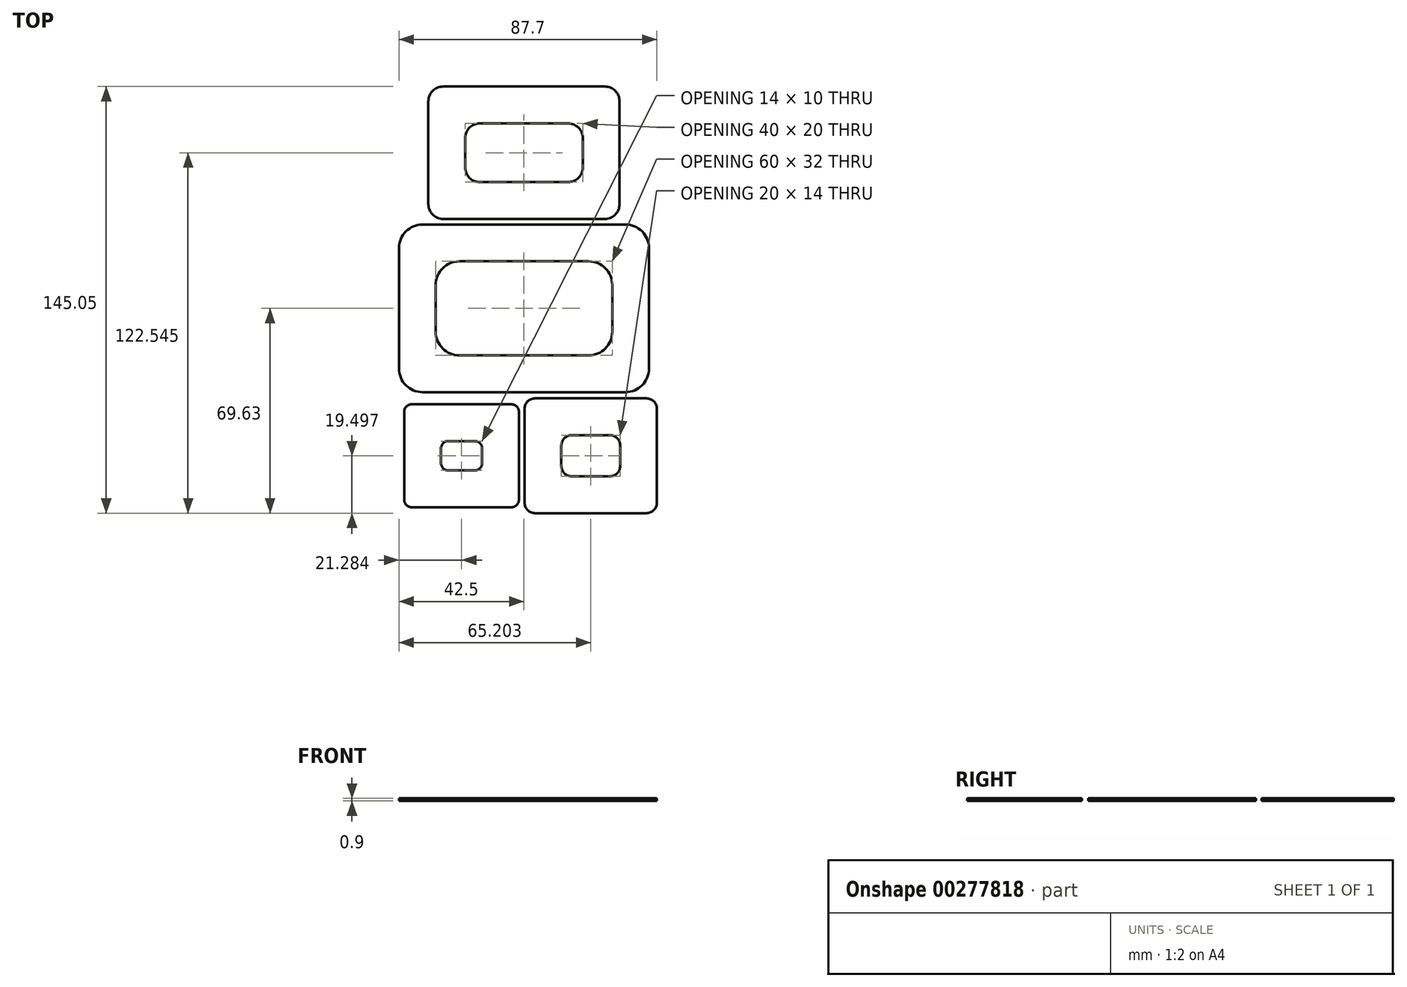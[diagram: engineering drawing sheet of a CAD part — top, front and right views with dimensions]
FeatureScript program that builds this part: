
annotation { "Feature Type Name" : "Feature", "Feature Type Description" : "" }
export const myFeature = defineFeature(function(context is Context, id is Id, definition is map)
    precondition{}
    {
        {
            var Q0;
            Q0=qCreatedBy(makeId("Top.planeOp"),FACE);
            var sketch = newSketch(context, id + "F0", { "sketchPlane" : qUnion([Q0])});
            skLineSegment(sketch, "E0.bottom", {"start": v(22, -16) * mm, "end": v(-22, -16) * mm});
            skLineSegment(sketch, "E0.top", {"start": v(22, 16) * mm, "end": v(-22, 16) * mm});
            skLineSegment(sketch, "E0.left", {"start": v(30, -8) * mm, "end": v(30, 8) * mm});
            skLineSegment(sketch, "E0.right", {"start": v(-30, -8) * mm, "end": v(-30, 8) * mm});
            skPoint(sketch, "E0.middle", {"position": v(0, 0) * mm});
            skPoint(sketch, "E1.visualSharp", {"position": v(-30, -16) * mm});
            skArc(sketch, "E1.filletArc", {"start": v(-30, -8) * mm, "mid": v(-27.66, -13.66) * mm, "end": v(-22, -16) * mm});
            skPoint(sketch, "E2.visualSharp", {"position": v(30, 16) * mm});
            skArc(sketch, "E2.filletArc", {"start": v(30, 8) * mm, "mid": v(27.66, 13.66) * mm, "end": v(22, 16) * mm});
            skPoint(sketch, "E3.visualSharp", {"position": v(30, -16) * mm});
            skArc(sketch, "E3.filletArc", {"start": v(22, -16) * mm, "mid": v(27.66, -13.66) * mm, "end": v(30, -8) * mm});
            skPoint(sketch, "E4.visualSharp", {"position": v(-30, 16) * mm});
            skArc(sketch, "E4.filletArc", {"start": v(-22, 16) * mm, "mid": v(-27.66, 13.66) * mm, "end": v(-30, 8) * mm});
            skLineSegment(sketch, "E5.bottom", {"start": v(34.5, -28.5) * mm, "end": v(-34.5, -28.5) * mm});
            skLineSegment(sketch, "E5.top", {"start": v(34.5, 28.5) * mm, "end": v(-34.5, 28.5) * mm});
            skLineSegment(sketch, "E5.left", {"start": v(42.5, -20.5) * mm, "end": v(42.5, 20.5) * mm});
            skLineSegment(sketch, "E5.right", {"start": v(-42.5, -20.5) * mm, "end": v(-42.5, 20.5) * mm});
            skPoint(sketch, "E6.visualSharp", {"position": v(-42.5, 28.5) * mm});
            skArc(sketch, "E6.filletArc", {"start": v(-34.5, 28.5) * mm, "mid": v(-40.16, 26.16) * mm, "end": v(-42.5, 20.5) * mm});
            skPoint(sketch, "E7.visualSharp", {"position": v(42.5, 28.5) * mm});
            skArc(sketch, "E7.filletArc", {"start": v(42.5, 20.5) * mm, "mid": v(40.16, 26.16) * mm, "end": v(34.5, 28.5) * mm});
            skPoint(sketch, "E8.visualSharp", {"position": v(42.5, -28.5) * mm});
            skArc(sketch, "E8.filletArc", {"start": v(34.5, -28.5) * mm, "mid": v(40.16, -26.16) * mm, "end": v(42.5, -20.5) * mm});
            skPoint(sketch, "E9.visualSharp", {"position": v(-42.5, -28.5) * mm});
            skArc(sketch, "E9.filletArc", {"start": v(-42.5, -20.5) * mm, "mid": v(-40.16, -26.16) * mm, "end": v(-34.5, -28.5) * mm});
            skLineSegment(sketch, "E10.bottom", {"start": v(27.5, 30.42) * mm, "end": v(-27.5, 30.42) * mm});
            skLineSegment(sketch, "E10.top", {"start": v(27.5, 75.42) * mm, "end": v(-27.5, 75.42) * mm});
            skLineSegment(sketch, "E10.left", {"start": v(32.5, 35.42) * mm, "end": v(32.5, 70.42) * mm});
            skLineSegment(sketch, "E10.right", {"start": v(-32.5, 35.42) * mm, "end": v(-32.5, 70.42) * mm});
            skPoint(sketch, "E10.middle", {"position": v(0, 52.92) * mm});
            skLineSegment(sketch, "E11.bottom", {"start": v(15, 42.92) * mm, "end": v(-15, 42.92) * mm});
            skLineSegment(sketch, "E11.top", {"start": v(15, 62.92) * mm, "end": v(-15, 62.92) * mm});
            skLineSegment(sketch, "E11.left", {"start": v(20, 47.92) * mm, "end": v(20, 57.92) * mm});
            skLineSegment(sketch, "E11.right", {"start": v(-20, 47.92) * mm, "end": v(-20, 57.92) * mm});
            skPoint(sketch, "E12.visualSharp", {"position": v(-20, 62.92) * mm});
            skArc(sketch, "E12.filletArc", {"start": v(-15, 62.92) * mm, "mid": v(-18.54, 61.45) * mm, "end": v(-20, 57.92) * mm});
            skPoint(sketch, "E13.visualSharp", {"position": v(20, 42.92) * mm});
            skArc(sketch, "E13.filletArc", {"start": v(15, 42.92) * mm, "mid": v(18.54, 44.38) * mm, "end": v(20, 47.92) * mm});
            skPoint(sketch, "E14.visualSharp", {"position": v(32.5, 30.42) * mm});
            skArc(sketch, "E14.filletArc", {"start": v(27.5, 30.42) * mm, "mid": v(31.04, 31.88) * mm, "end": v(32.5, 35.42) * mm});
            skPoint(sketch, "E15.visualSharp", {"position": v(20, 62.92) * mm});
            skArc(sketch, "E15.filletArc", {"start": v(20, 57.92) * mm, "mid": v(18.54, 61.45) * mm, "end": v(15, 62.92) * mm});
            skPoint(sketch, "E16.visualSharp", {"position": v(-32.5, 30.42) * mm});
            skArc(sketch, "E16.filletArc", {"start": v(-32.5, 35.42) * mm, "mid": v(-31.04, 31.88) * mm, "end": v(-27.5, 30.42) * mm});
            skPoint(sketch, "E17.visualSharp", {"position": v(-32.5, 75.42) * mm});
            skArc(sketch, "E17.filletArc", {"start": v(-27.5, 75.42) * mm, "mid": v(-31.04, 73.95) * mm, "end": v(-32.5, 70.42) * mm});
            skPoint(sketch, "E18.visualSharp", {"position": v(32.5, 75.42) * mm});
            skArc(sketch, "E18.filletArc", {"start": v(32.5, 70.42) * mm, "mid": v(31.04, 73.95) * mm, "end": v(27.5, 75.42) * mm});
            skPoint(sketch, "E19.visualSharp", {"position": v(-20, 42.92) * mm});
            skArc(sketch, "E19.filletArc", {"start": v(-20, 47.92) * mm, "mid": v(-18.54, 44.38) * mm, "end": v(-15, 42.92) * mm});
            skLineSegment(sketch, "E20.bottom", {"start": v(41.7, -69.63) * mm, "end": v(3.7, -69.63) * mm});
            skLineSegment(sketch, "E20.top", {"start": v(41.7, -30.63) * mm, "end": v(3.7, -30.63) * mm});
            skLineSegment(sketch, "E20.left", {"start": v(45.2, -66.13) * mm, "end": v(45.2, -34.13) * mm});
            skLineSegment(sketch, "E20.right", {"start": v(0.2, -66.13) * mm, "end": v(0.2, -34.13) * mm});
            skPoint(sketch, "E20.middle", {"position": v(22.7, -50.13) * mm});
            skLineSegment(sketch, "E21.bottom", {"start": v(29.2, -57.13) * mm, "end": v(16.2, -57.13) * mm});
            skLineSegment(sketch, "E21.top", {"start": v(29.2, -43.13) * mm, "end": v(16.2, -43.13) * mm});
            skLineSegment(sketch, "E21.left", {"start": v(32.7, -53.63) * mm, "end": v(32.7, -46.63) * mm});
            skLineSegment(sketch, "E21.right", {"start": v(12.7, -53.63) * mm, "end": v(12.7, -46.63) * mm});
            skPoint(sketch, "E22.visualSharp", {"position": v(0.2, -30.63) * mm});
            skArc(sketch, "E22.filletArc", {"start": v(3.7, -30.63) * mm, "mid": v(1.23, -31.66) * mm, "end": v(0.2, -34.13) * mm});
            skPoint(sketch, "E23.visualSharp", {"position": v(0.2, -69.63) * mm});
            skArc(sketch, "E23.filletArc", {"start": v(0.2, -66.13) * mm, "mid": v(1.23, -68.6) * mm, "end": v(3.7, -69.63) * mm});
            skPoint(sketch, "E24.visualSharp", {"position": v(45.2, -69.63) * mm});
            skArc(sketch, "E24.filletArc", {"start": v(41.7, -69.63) * mm, "mid": v(44.18, -68.6) * mm, "end": v(45.2, -66.13) * mm});
            skPoint(sketch, "E25.visualSharp", {"position": v(45.2, -30.63) * mm});
            skArc(sketch, "E25.filletArc", {"start": v(45.2, -34.13) * mm, "mid": v(44.18, -31.66) * mm, "end": v(41.7, -30.63) * mm});
            skPoint(sketch, "E26.visualSharp", {"position": v(32.7, -43.13) * mm});
            skArc(sketch, "E26.filletArc", {"start": v(32.7, -46.63) * mm, "mid": v(31.68, -44.16) * mm, "end": v(29.2, -43.13) * mm});
            skPoint(sketch, "E27.visualSharp", {"position": v(12.7, -43.13) * mm});
            skArc(sketch, "E27.filletArc", {"start": v(16.2, -43.13) * mm, "mid": v(13.73, -44.16) * mm, "end": v(12.7, -46.63) * mm});
            skPoint(sketch, "E28.visualSharp", {"position": v(32.7, -57.13) * mm});
            skArc(sketch, "E28.filletArc", {"start": v(29.2, -57.13) * mm, "mid": v(31.68, -56.1) * mm, "end": v(32.7, -53.63) * mm});
            skPoint(sketch, "E29.visualSharp", {"position": v(12.7, -57.13) * mm});
            skArc(sketch, "E29.filletArc", {"start": v(12.7, -53.63) * mm, "mid": v(13.73, -56.1) * mm, "end": v(16.2, -57.13) * mm});
            skLineSegment(sketch, "E30.bottom", {"start": v(-4.22, -67.63) * mm, "end": v(-38.22, -67.63) * mm});
            skLineSegment(sketch, "E30.top", {"start": v(-4.22, -32.63) * mm, "end": v(-38.22, -32.63) * mm});
            skLineSegment(sketch, "E30.left", {"start": v(-1.72, -65.13) * mm, "end": v(-1.72, -35.13) * mm});
            skLineSegment(sketch, "E30.right", {"start": v(-40.72, -65.13) * mm, "end": v(-40.72, -35.13) * mm});
            skPoint(sketch, "E30.middle", {"position": v(-21.22, -50.13) * mm});
            skPoint(sketch, "E30.middle.positionSnap0", {"position": v(12.7, -50.13) * mm});
            skPoint(sketch, "E30.centerSnap0", {"position": v(12.7, -50.13) * mm});
            skLineSegment(sketch, "E31.bottom", {"start": v(-16.72, -55.13) * mm, "end": v(-25.72, -55.13) * mm});
            skLineSegment(sketch, "E31.top", {"start": v(-16.72, -45.13) * mm, "end": v(-25.72, -45.13) * mm});
            skLineSegment(sketch, "E31.left", {"start": v(-14.22, -52.63) * mm, "end": v(-14.22, -47.63) * mm});
            skLineSegment(sketch, "E31.right", {"start": v(-28.22, -52.63) * mm, "end": v(-28.22, -47.63) * mm});
            skPoint(sketch, "E32.visualSharp", {"position": v(-40.72, -32.63) * mm});
            skArc(sketch, "E32.filletArc", {"start": v(-38.22, -32.63) * mm, "mid": v(-39.98, -33.37) * mm, "end": v(-40.72, -35.13) * mm});
            skPoint(sketch, "E33.visualSharp", {"position": v(-1.72, -32.63) * mm});
            skArc(sketch, "E33.filletArc", {"start": v(-1.72, -35.13) * mm, "mid": v(-2.45, -33.37) * mm, "end": v(-4.22, -32.63) * mm});
            skPoint(sketch, "E34.visualSharp", {"position": v(-1.72, -67.63) * mm});
            skArc(sketch, "E34.filletArc", {"start": v(-4.22, -67.63) * mm, "mid": v(-2.45, -66.9) * mm, "end": v(-1.72, -65.13) * mm});
            skPoint(sketch, "E35.visualSharp", {"position": v(-40.72, -67.63) * mm});
            skArc(sketch, "E35.filletArc", {"start": v(-40.72, -65.13) * mm, "mid": v(-39.98, -66.9) * mm, "end": v(-38.22, -67.63) * mm});
            skPoint(sketch, "E36.visualSharp", {"position": v(-28.22, -55.13) * mm});
            skArc(sketch, "E36.filletArc", {"start": v(-28.22, -52.63) * mm, "mid": v(-27.48, -54.4) * mm, "end": v(-25.72, -55.13) * mm});
            skPoint(sketch, "E37.visualSharp", {"position": v(-28.22, -45.13) * mm});
            skArc(sketch, "E37.filletArc", {"start": v(-25.72, -45.13) * mm, "mid": v(-27.48, -45.87) * mm, "end": v(-28.22, -47.63) * mm});
            skPoint(sketch, "E38.visualSharp", {"position": v(-14.22, -45.13) * mm});
            skArc(sketch, "E38.filletArc", {"start": v(-14.22, -47.63) * mm, "mid": v(-14.95, -45.87) * mm, "end": v(-16.72, -45.13) * mm});
            skPoint(sketch, "E39.visualSharp", {"position": v(-14.22, -55.13) * mm});
            skArc(sketch, "E39.filletArc", {"start": v(-16.72, -55.13) * mm, "mid": v(-14.95, -54.4) * mm, "end": v(-14.22, -52.63) * mm});
            skSolve(sketch);
        }
        {
            var Q0;
            Q0=makeQuery(id+"F0.imprint","IMPRINT",FACE,{"disambiguationData":[TD([[makeQuery(id+"F0.imprint","IMPRINT",EDGE,{"derivedFrom":sQuery(id+"F0.wireOp",EDGE,"E30.bottom")}),-1.0]])]});
            var Q1;
            Q1=makeQuery(id+"F0.imprint","IMPRINT",FACE,{"disambiguationData":[TD([[makeQuery(id+"F0.imprint","IMPRINT",EDGE,{"derivedFrom":sQuery(id+"F0.wireOp",EDGE,"E20.bottom")}),-1.0]])]});
            var Q2;
            Q2=makeQuery(id+"F0.imprint","IMPRINT",FACE,{"disambiguationData":[TD([[makeQuery(id+"F0.imprint","IMPRINT",EDGE,{"derivedFrom":sQuery(id+"F0.wireOp",EDGE,"E0.bottom")}),1.0]])]});
            var Q3;
            Q3=makeQuery(id+"F0.imprint","IMPRINT",FACE,{"disambiguationData":[TD([[makeQuery(id+"F0.imprint","IMPRINT",EDGE,{"derivedFrom":sQuery(id+"F0.wireOp",EDGE,"E10.bottom")}),-1.0]])]});
            extrude(context, id + "F1", {"entities" : qUnion([Q0, Q1, Q2, Q3]), "depth" : 0.9 * mm});
        }
    });
